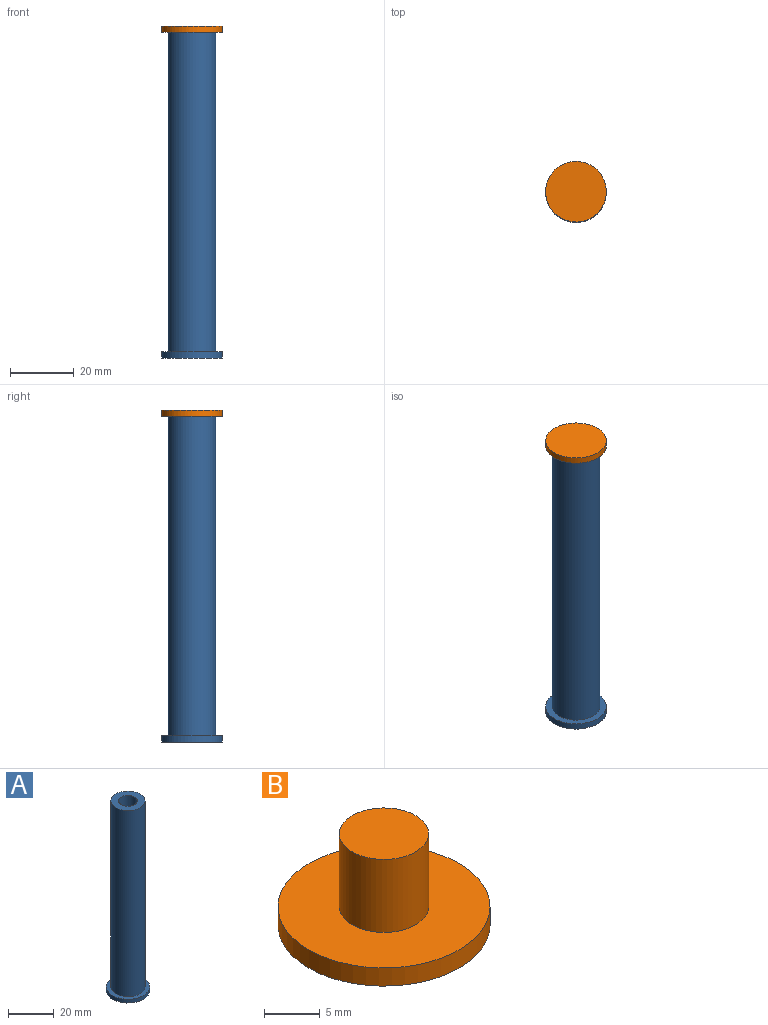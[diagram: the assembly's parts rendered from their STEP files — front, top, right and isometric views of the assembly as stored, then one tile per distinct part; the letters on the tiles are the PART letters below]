
ASSEMBLY  parts=2 mates=1
PART A: 7 faces, bbox 19x19x102 mm
  f0: plane 19x19mm, normal (0,0,-1), area 283.5mm2, adj f1
  f1: cylinder r=9.5mm len=19mm, axis (0,0,-1), area 119.4mm2, adj f0,f2
  f2: plane 19x19mm, normal (0,0,1), area 106.8mm2, adj f1,f3
  f3: cylinder r=7.5mm len=100mm, axis (0,0,-1), area 4712.4mm2, adj f2,f4
  f4: plane 15x15mm, normal (0,0,1), area 123.9mm2, adj f3,f5
  f5: cylinder r=4.1mm len=8.2mm, axis (0,0,1), area 211.2mm2, adj f4,f6
  f6: plane 8.2x8.2mm, normal (0,0,1), area 52.8mm2, adj f5
PART B: 5 faces, bbox 19x19x10 mm
  f0: plane 19x19mm, normal (0,0,-1), area 283.5mm2, adj f1
  f1: cylinder r=9.5mm len=19mm, axis (0,0,-1), area 119.4mm2, adj f0,f2
  f2: plane 19x19mm, normal (0,0,1), area 233.3mm2, adj f1,f3
  f3: cylinder r=4mm len=8mm, axis (0,0,-1), area 201.1mm2, adj f2,f4
  f4: plane 8x8mm, normal (0,0,1), area 50.3mm2, adj f3
PLACE A t=(-22.49,-20.67,-16.52)mm
PLACE B rot(axis=(1,0,0),180deg) t=(-22.49,-20.67,87.48)mm
MATE fastened B.f1 <-> A.f1  axis (0,0,-1) through (-22.49,-20.67,85.48)mm
